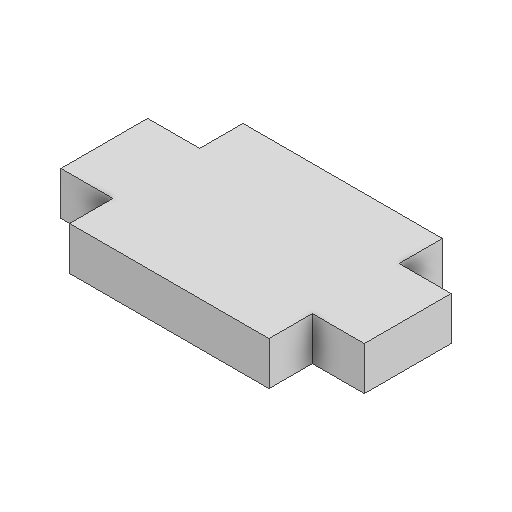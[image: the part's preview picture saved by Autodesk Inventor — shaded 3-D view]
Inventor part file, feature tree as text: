
AUTODESK INVENTOR PART (.ipt)
format: ipt  version: 2022 (Build 260153000, 153)  size: 114,176 bytes
history: native  units: mm
features: other x4, extrude x2, sketch x2, reference x2
ambient origin geometry x8: Origin, YZ Plane, XZ Plane, XY Plane, X Axis, Y Axis, Z Axis, Center Point
bodies: Body1 (feature_tree)
feature tree (10):
  other  "Твердое тело1"
  extrude  "Выдавливание1"  Depth=10.0mm
  extrude  "Выдавливание2"  Depth=20.0mm
  sketch  "Эскиз1"
  sketch  "Эскиз2"
  reference  "Ссылка1"
  reference  "Ссылка2"
  other  "<userpath>\Documents\Inventor\Файлы Inventor\Конвейр без шпилек сборка.iam"
  other  "Конвейр без шпилек сборка.iam"
  other  "Стенка конвейера:1"
